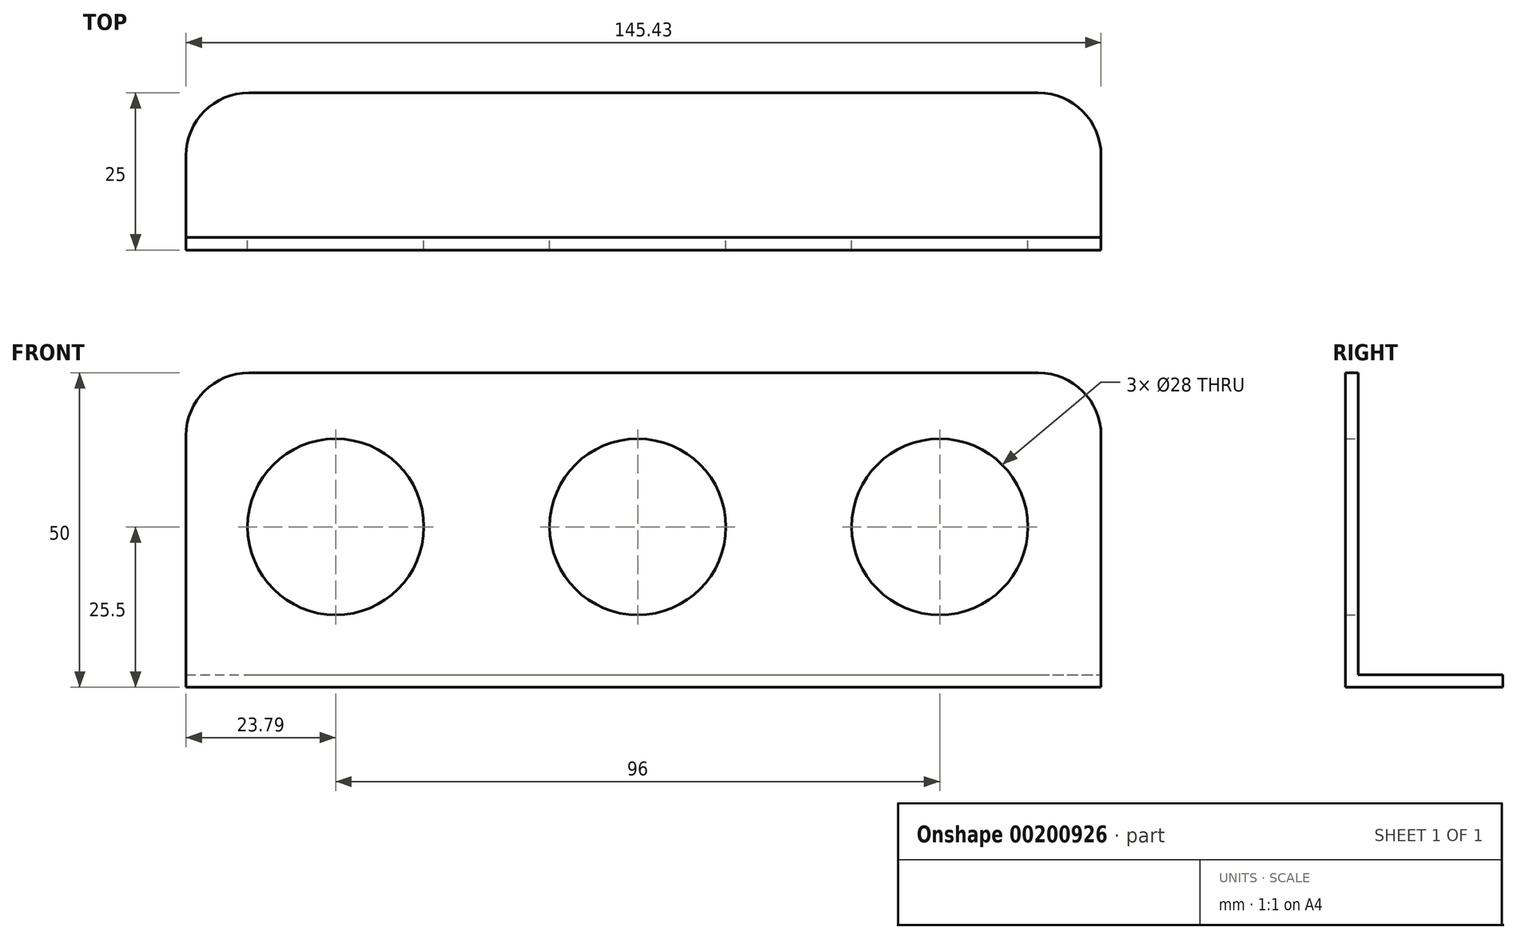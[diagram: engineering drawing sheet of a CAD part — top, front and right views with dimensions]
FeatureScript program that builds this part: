
annotation { "Feature Type Name" : "Feature", "Feature Type Description" : "" }
export const myFeature = defineFeature(function(context is Context, id is Id, definition is map)
    precondition{}
    {
        {
            var Q0;
            Q0=qCreatedBy(makeId("Front.planeOp"),FACE);
            var sketch = newSketch(context, id + "F0", { "sketchPlane" : qUnion([Q0])});
            skCircle(sketch, "E0", {"center": v(0, 0) * mm, "radius": 14 * mm});
            skCircle(sketch, "E1", {"center": v(-48, 0) * mm, "radius": 14 * mm});
            skCircle(sketch, "E2", {"center": v(48, 0) * mm, "radius": 14 * mm});
            skLineSegment(sketch, "E3.bottom", {"start": v(-71.79, 24.5) * mm, "end": v(73.64, 24.5) * mm});
            skLineSegment(sketch, "E3.top", {"start": v(-71.79, -23.5) * mm, "end": v(73.64, -23.5) * mm});
            skLineSegment(sketch, "E3.left", {"start": v(-71.79, 24.5) * mm, "end": v(-71.79, -23.5) * mm});
            skLineSegment(sketch, "E3.right", {"start": v(73.64, 24.5) * mm, "end": v(73.64, -23.5) * mm});
            skSolve(sketch);
        }
        {
            var Q0;
            Q0=makeQuery(id+"F0.imprint","IMPRINT",FACE,{"disambiguationData":[TD([[makeQuery(id+"F0.imprint","IMPRINT",EDGE,{"derivedFrom":sQuery(id+"F0.wireOp",EDGE,"E0")}),-1.0]])]});
            extrude(context, id + "F1", {"entities" : qUnion([Q0]), "depth" : 2 * mm});
        }
        {
            var Q0;
            Q0=makeQuery(id+"F1.opExtrude","SWEPT_FACE",FACE,{"disambiguationData":[OSD([sQuery(id+"F0.wireOp",EDGE,"E3.top")])]});
            cPlane(context, id + "F2", {"entities" : qUnion([Q0]), "cplaneType" : CPlaneType.OFFSET, "offset" : 0 * mm, "width" : 150 * mm, "height" : 150 * mm});
        }
        {
            var Q0;
            Q0=makeQuery(id+"F1.opExtrude","SWEPT_EDGE",EDGE,{"disambiguationData":[OSD([sQuery(id+"F0.wireOp",EDGE,"E3.bottom"),sQuery(id+"F0.wireOp",EDGE,"E3.right")])]});
            var Q1;
            Q1=makeQuery(id+"F1.opExtrude","SWEPT_EDGE",EDGE,{"disambiguationData":[OSD([sQuery(id+"F0.wireOp",EDGE,"E3.bottom"),sQuery(id+"F0.wireOp",EDGE,"E3.left")])]});
            var Q2;
            Q2=makeQuery(id+"FgF89ux4eGTzrb9_1.opExtrude","SWEPT_EDGE",EDGE,{"disambiguationData":[OSD([sQuery(id+"FoJdqqJvLjXBuRn_1.wireOp",EDGE,"RK9JkqSX-nWgc-xS1n-C8Iq-Fm5sdvoT2Pum.top"),sQuery(id+"FoJdqqJvLjXBuRn_1.wireOp",EDGE,"RK9JkqSX-nWgc-xS1n-C8Iq-Fm5sdvoT2Pum.right")])]});
            var Q3;
            Q3=makeQuery(id+"FgF89ux4eGTzrb9_1.opExtrude","SWEPT_EDGE",EDGE,{"disambiguationData":[OSD([sQuery(id+"FoJdqqJvLjXBuRn_1.wireOp",EDGE,"RK9JkqSX-nWgc-xS1n-C8Iq-Fm5sdvoT2Pum.top"),sQuery(id+"FoJdqqJvLjXBuRn_1.wireOp",EDGE,"RK9JkqSX-nWgc-xS1n-C8Iq-Fm5sdvoT2Pum.left")])]});
            fillet(context, id + "F3", {"entities" : qUnion([Q0, Q1, Q2, Q3]), "radius" : 10 * mm, "tangentPropagation" : true, "allowEdgeOverflow" : false});
        }
        {
            var Q0;
            Q0=qCreatedBy(id+"F2.planeOp",FACE);
            var sketch = newSketch(context, id + "F4", { "sketchPlane" : qUnion([Q0])});
            skLineSegment(sketch, "E4.0", {"start": v(-71.79, 2) * mm, "end": v(73.64, 2) * mm});
            skLineSegment(sketch, "E5.top", {"start": v(-71.79, -23) * mm, "end": v(73.64, -23) * mm});
            skLineSegment(sketch, "E5.left", {"start": v(-71.79, 2) * mm, "end": v(-71.79, -23) * mm});
            skLineSegment(sketch, "E5.right", {"start": v(73.64, 2) * mm, "end": v(73.64, -23) * mm});
            skSolve(sketch);
        }
        {
            var Q0;
            Q0=makeQuery(id+"F4.imprint","IMPRINT",FACE,{"disambiguationData":[TD([[makeQuery(id+"F4.imprint","IMPRINT",EDGE,{"derivedFrom":sQuery(id+"F4.wireOp",EDGE,"E4.0")}),-1.0]])]});
            extrude(context, id + "F5", {"entities" : qUnion([Q0]), "operationType" : NewBodyOperationType.ADD, "depth" : 2 * mm});
        }
        {
            var Q0;
            Q0=makeQuery(id+"F5.opExtrude","SWEPT_EDGE",EDGE,{"disambiguationData":[OSD([sQuery(id+"F4.wireOp",EDGE,"E5.top"),sQuery(id+"F4.wireOp",EDGE,"E5.left")])]});
            var Q1;
            Q1=makeQuery(id+"F5.opExtrude","SWEPT_EDGE",EDGE,{"disambiguationData":[OSD([sQuery(id+"F4.wireOp",EDGE,"E5.top"),sQuery(id+"F4.wireOp",EDGE,"E5.right")])]});
            fillet(context, id + "F6", {"entities" : qUnion([Q0, Q1]), "radius" : 10 * mm, "tangentPropagation" : true, "allowEdgeOverflow" : false});
        }
    });
